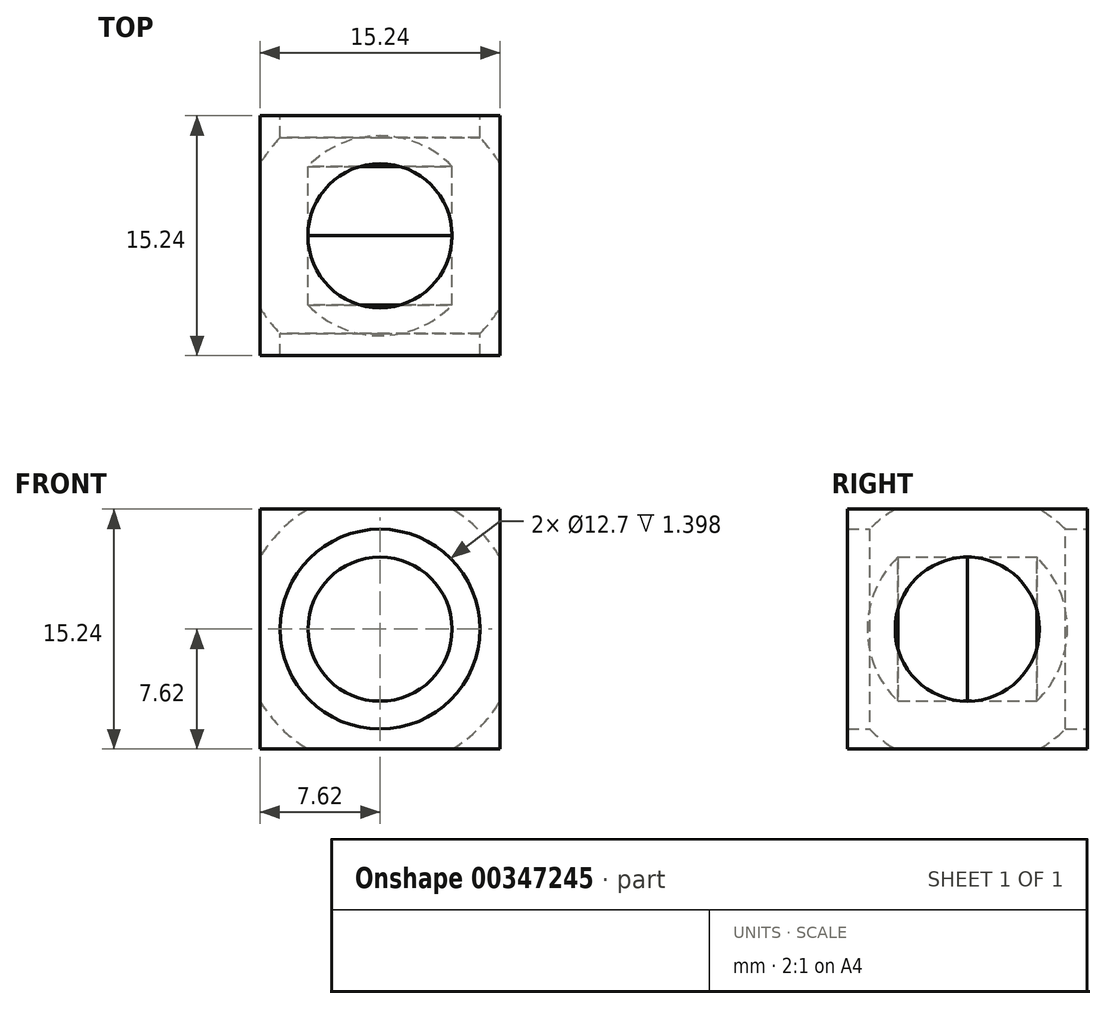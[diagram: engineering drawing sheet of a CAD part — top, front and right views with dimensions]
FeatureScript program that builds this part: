
annotation { "Feature Type Name" : "Feature", "Feature Type Description" : "" }
export const myFeature = defineFeature(function(context is Context, id is Id, definition is map)
    precondition{}
    {
        {
            var Q0;
            Q0=qCreatedBy(makeId("Front.planeOp"),FACE);
            var sketch = newSketch(context, id + "F0", { "sketchPlane" : qUnion([Q0])});
            skLineSegment(sketch, "E0.bottom", {"start": v(7.62, -7.62) * mm, "end": v(-7.62, -7.62) * mm});
            skLineSegment(sketch, "E0.top", {"start": v(7.62, 7.62) * mm, "end": v(-7.62, 7.62) * mm});
            skLineSegment(sketch, "E0.left", {"start": v(7.62, -7.62) * mm, "end": v(7.62, 7.62) * mm});
            skLineSegment(sketch, "E0.right", {"start": v(-7.62, -7.62) * mm, "end": v(-7.62, 7.62) * mm});
            skPoint(sketch, "E0.middle", {"position": v(0, 0) * mm});
            skCircle(sketch, "E1", {"center": v(0, 0) * mm, "radius": 8.89 * mm});
            skLineSegment(sketch, "E2", {"start": v(0, 11.6) * mm, "end": v(0, -9.09) * mm, "construction": true});
            skPoint(sketch, "E2.startSnap0", {"position": v(0, 7.62) * mm});
            skPoint(sketch, "E2.endSnap0", {"position": v(0, -7.62) * mm});
            skLineSegment(sketch, "E3", {"start": v(0, 8.89) * mm, "end": v(0, -8.89) * mm});
            skCircle(sketch, "E4", {"center": v(0, 0) * mm, "radius": 6.35 * mm});
            skCircle(sketch, "E5", {"center": v(0, 0) * mm, "radius": 4.57 * mm});
            skSolve(sketch);
        }
        {
            var Q0;
            {var subQ0=sQuery(id+"F0.wireOp",EDGE,"E0.left");var subQ1=sQuery(id+"F0.wireOp",EDGE,"E0.top");var subQ2=makeQuery(id+"F0.imprint","INTERSECT",VERTEX,{"derivedFrom":[subQ1,subQ0]});Q0=makeQuery(id+"F0.imprint","IMPRINT",FACE,{"disambiguationData":[TD([[makeQuery(id+"F0.imprint","IMPRINT",EDGE,{"disambiguationData":[TD([[subQ2,-1.0]])],"derivedFrom":subQ1}),1.0]])]});}
            var Q1;
            {var subQ0=sQuery(id+"F0.wireOp",EDGE,"E1");var subQ10=sQuery(id+"F0.wireOp",EDGE,"E0.bottom");var subQ13=makeQuery(id+"F0.imprint","INTERSECT",VERTEX,{"disambiguationData":[OD(0.0)],"derivedFrom":[subQ10,subQ0]});Q1=makeQuery(id+"F0.imprint","IMPRINT",FACE,{"disambiguationData":[TD([[makeQuery(id+"F0.imprint","IMPRINT",EDGE,{"disambiguationData":[TD([[subQ13,-1.0]])],"derivedFrom":subQ10}),-1.0]])]});}
            var Q2;
            {var subQ0=sQuery(id+"F0.wireOp",EDGE,"E0.left");var subQ1=sQuery(id+"F0.wireOp",EDGE,"E0.bottom");var subQ2=makeQuery(id+"F0.imprint","INTERSECT",VERTEX,{"derivedFrom":[subQ1,subQ0]});Q2=makeQuery(id+"F0.imprint","IMPRINT",FACE,{"disambiguationData":[TD([[makeQuery(id+"F0.imprint","IMPRINT",EDGE,{"disambiguationData":[TD([[subQ2,-1.0]])],"derivedFrom":subQ1}),-1.0]])]});}
            var Q3;
            {var subQ0=sQuery(id+"F0.wireOp",EDGE,"E1");var subQ8=sQuery(id+"F0.wireOp",EDGE,"E0.bottom");var subQ9=makeQuery(id+"F0.imprint","INTERSECT",VERTEX,{"disambiguationData":[OD(1.0)],"derivedFrom":[subQ8,subQ0]});Q3=makeQuery(id+"F0.imprint","IMPRINT",FACE,{"disambiguationData":[TD([[makeQuery(id+"F0.imprint","IMPRINT",EDGE,{"disambiguationData":[TD([[subQ9,1.0]])],"derivedFrom":subQ8}),-1.0]])]});}
            var Q4;
            {var subQ0=sQuery(id+"F0.wireOp",EDGE,"E0.right");var subQ1=sQuery(id+"F0.wireOp",EDGE,"E0.top");var subQ2=makeQuery(id+"F0.imprint","INTERSECT",VERTEX,{"derivedFrom":[subQ1,subQ0]});Q4=makeQuery(id+"F0.imprint","IMPRINT",FACE,{"disambiguationData":[TD([[makeQuery(id+"F0.imprint","IMPRINT",EDGE,{"disambiguationData":[TD([[subQ2,1.0]])],"derivedFrom":subQ1}),1.0]])]});}
            var Q5;
            {var subQ0=sQuery(id+"F0.wireOp",EDGE,"E0.right");var subQ1=sQuery(id+"F0.wireOp",EDGE,"E0.bottom");var subQ2=makeQuery(id+"F0.imprint","INTERSECT",VERTEX,{"derivedFrom":[subQ1,subQ0]});Q5=makeQuery(id+"F0.imprint","IMPRINT",FACE,{"disambiguationData":[TD([[makeQuery(id+"F0.imprint","IMPRINT",EDGE,{"disambiguationData":[TD([[subQ2,1.0]])],"derivedFrom":subQ1}),-1.0]])]});}
            var Q6;
            {var subQ0=sQuery(id+"F0.wireOp",EDGE,"E4");var subQ1=sQuery(id+"F0.wireOp",EDGE,"E3");var subQ2=makeQuery(id+"F0.imprint","INTERSECT",VERTEX,{"disambiguationData":[OD(0.0)],"derivedFrom":[subQ1,subQ0]});Q6=makeQuery(id+"F0.imprint","IMPRINT",FACE,{"disambiguationData":[TD([[makeQuery(id+"F0.imprint","IMPRINT",EDGE,{"disambiguationData":[TD([[subQ2,-1.0]])],"derivedFrom":subQ1}),-1.0]])]});}
            var Q7;
            {var subQ0=sQuery(id+"F0.wireOp",EDGE,"E4");var subQ1=sQuery(id+"F0.wireOp",EDGE,"E3");var subQ2=makeQuery(id+"F0.imprint","INTERSECT",VERTEX,{"disambiguationData":[OD(0.0)],"derivedFrom":[subQ1,subQ0]});Q7=makeQuery(id+"F0.imprint","IMPRINT",FACE,{"disambiguationData":[TD([[makeQuery(id+"F0.imprint","IMPRINT",EDGE,{"disambiguationData":[TD([[subQ2,-1.0]])],"derivedFrom":subQ1}),1.0]])]});}
            var Q8;
            {var subQ0=sQuery(id+"F0.wireOp",EDGE,"E5");var subQ1=sQuery(id+"F0.wireOp",EDGE,"E3");var subQ2=makeQuery(id+"F0.imprint","INTERSECT",VERTEX,{"disambiguationData":[OD(0.0)],"derivedFrom":[subQ1,subQ0]});Q8=makeQuery(id+"F0.imprint","IMPRINT",FACE,{"disambiguationData":[TD([[makeQuery(id+"F0.imprint","IMPRINT",EDGE,{"disambiguationData":[TD([[subQ2,-1.0]])],"derivedFrom":subQ1}),1.0]])]});}
            var Q9;
            {var subQ0=sQuery(id+"F0.wireOp",EDGE,"E5");var subQ1=sQuery(id+"F0.wireOp",EDGE,"E3");var subQ2=makeQuery(id+"F0.imprint","INTERSECT",VERTEX,{"disambiguationData":[OD(0.0)],"derivedFrom":[subQ1,subQ0]});Q9=makeQuery(id+"F0.imprint","IMPRINT",FACE,{"disambiguationData":[TD([[makeQuery(id+"F0.imprint","IMPRINT",EDGE,{"disambiguationData":[TD([[subQ2,-1.0]])],"derivedFrom":subQ1}),-1.0]])]});}
            extrude(context, id + "F1", {"entities" : qUnion([Q0, Q1, Q2, Q3, Q4, Q5, Q6, Q7, Q8, Q9]), "endBound" : BoundingType.SYMMETRIC, "depth" : 15.24 * mm});
        }
        {
            var Q0;
            {var subQ0=sQuery(id+"F0.wireOp",EDGE,"E1");var subQ1=sQuery(id+"F0.wireOp",EDGE,"E0.bottom");var subQ2=makeQuery(id+"F0.imprint","INTERSECT",VERTEX,{"disambiguationData":[OD(0.0)],"derivedFrom":[subQ1,subQ0]});Q0=makeQuery(id+"F0.imprint","IMPRINT",FACE,{"disambiguationData":[TD([[makeQuery(id+"F0.imprint","IMPRINT",EDGE,{"disambiguationData":[TD([[subQ2,-1.0]])],"derivedFrom":subQ1}),1.0]])]});}
            var Q1;
            {var subQ0=sQuery(id+"F0.wireOp",EDGE,"E1");var subQ1=sQuery(id+"F0.wireOp",EDGE,"E0.top");var subQ2=makeQuery(id+"F0.imprint","INTERSECT",VERTEX,{"disambiguationData":[OD(0.0)],"derivedFrom":[subQ1,subQ0]});Q1=makeQuery(id+"F0.imprint","IMPRINT",FACE,{"disambiguationData":[TD([[makeQuery(id+"F0.imprint","IMPRINT",EDGE,{"disambiguationData":[TD([[subQ2,-1.0]])],"derivedFrom":subQ1}),-1.0]])]});}
            var Q2;
            {var subQ0=sQuery(id+"F0.wireOp",EDGE,"E1");var subQ10=sQuery(id+"F0.wireOp",EDGE,"E0.bottom");var subQ11=makeQuery(id+"F0.imprint","INTERSECT",VERTEX,{"disambiguationData":[OD(0.0)],"derivedFrom":[subQ10,subQ0]});Q2=makeQuery(id+"F0.imprint","IMPRINT",FACE,{"disambiguationData":[TD([[makeQuery(id+"F0.imprint","IMPRINT",EDGE,{"disambiguationData":[TD([[subQ11,-1.0]])],"derivedFrom":subQ10}),-1.0]])]});}
            var Q3;
            {var subQ0=sQuery(id+"F0.wireOp",EDGE,"E1");var subQ1=sQuery(id+"F0.wireOp",EDGE,"E0.left");var subQ2=makeQuery(id+"F0.imprint","INTERSECT",VERTEX,{"disambiguationData":[OD(0.0)],"derivedFrom":[subQ1,subQ0]});Q3=makeQuery(id+"F0.imprint","IMPRINT",FACE,{"disambiguationData":[TD([[makeQuery(id+"F0.imprint","IMPRINT",EDGE,{"disambiguationData":[TD([[subQ2,-1.0]])],"derivedFrom":subQ1}),-1.0]])]});}
            var Q4;
            {var subQ0=sQuery(id+"F0.wireOp",EDGE,"E5");var subQ1=sQuery(id+"F0.wireOp",EDGE,"E3");var subQ2=makeQuery(id+"F0.imprint","INTERSECT",VERTEX,{"disambiguationData":[OD(0.0)],"derivedFrom":[subQ1,subQ0]});Q4=makeQuery(id+"F0.imprint","IMPRINT",FACE,{"disambiguationData":[TD([[makeQuery(id+"F0.imprint","IMPRINT",EDGE,{"disambiguationData":[TD([[subQ2,-1.0]])],"derivedFrom":subQ1}),1.0]])]});}
            var Q5;
            Q5=sQuery(id+"F0.wireOp",EDGE,"E2");
            revolve(context, id + "F2", {"operationType" : NewBodyOperationType.REMOVE, "entities" : qUnion([Q0, Q1, Q2, Q3, Q4]), "axis" : qUnion([Q5]), "revolveType" : RevolveType.FULL, "oppositeDirection" : true});
        }
    });
